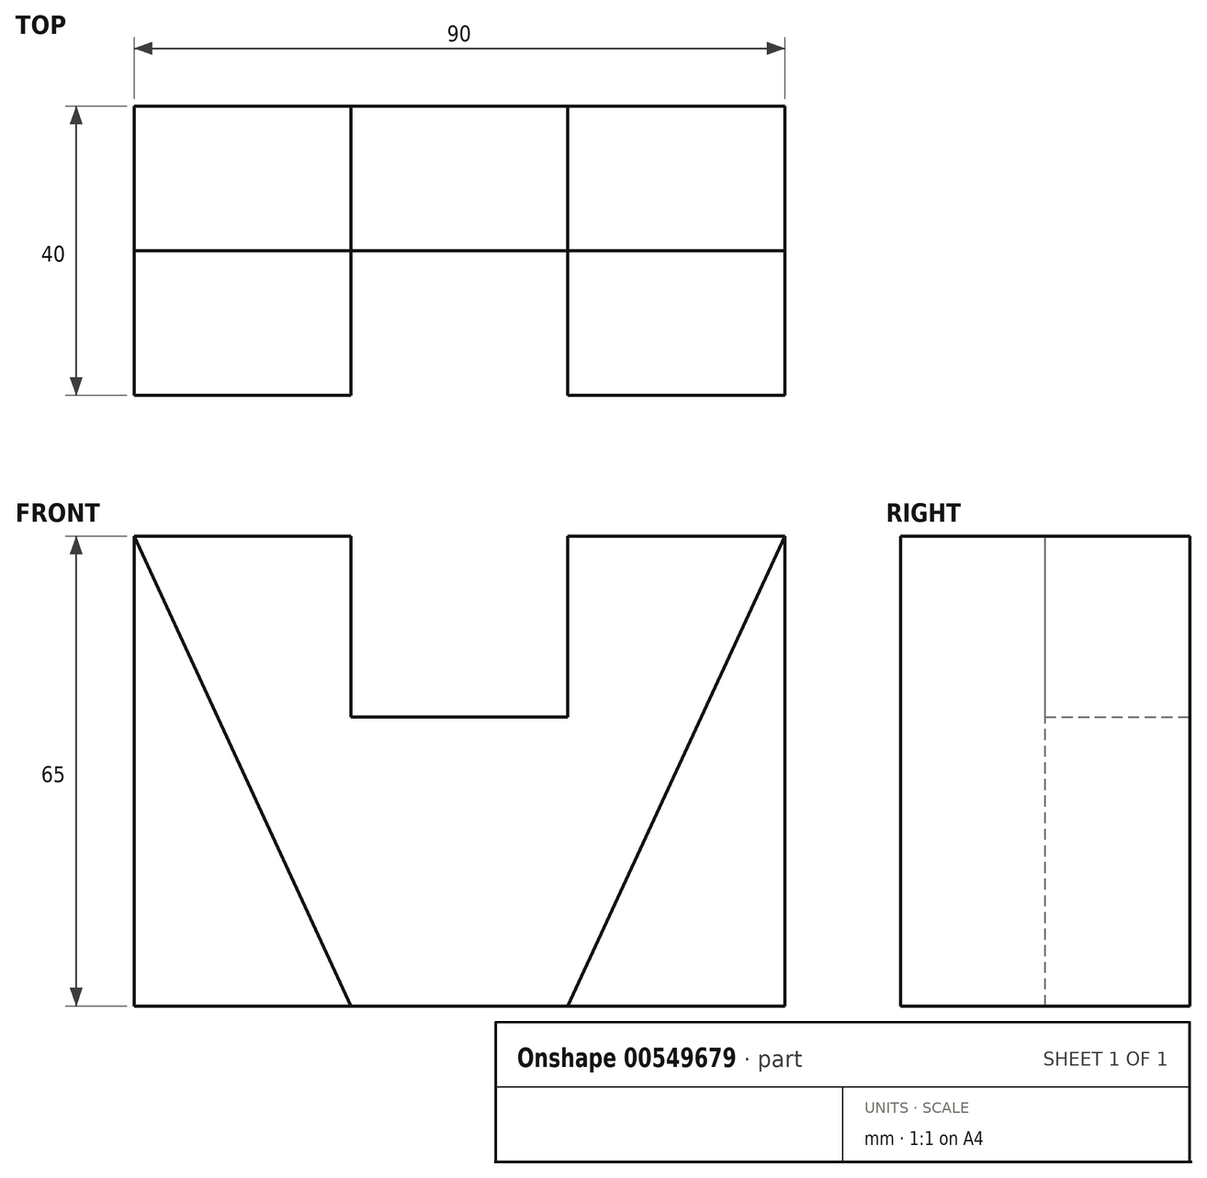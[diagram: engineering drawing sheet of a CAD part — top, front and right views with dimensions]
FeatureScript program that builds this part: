
annotation { "Feature Type Name" : "Feature", "Feature Type Description" : "" }
export const myFeature = defineFeature(function(context is Context, id is Id, definition is map)
    precondition{}
    {
        {
            var Q0;
            Q0=qCreatedBy(makeId("Front.planeOp"),FACE);
            var sketch = newSketch(context, id + "F0", { "sketchPlane" : qUnion([Q0])});
            skLineSegment(sketch, "E0.bottom", {"start": v(45, 32.5) * mm, "end": v(15, 32.5) * mm});
            skLineSegment(sketch, "E0.top", {"start": v(45, -32.5) * mm, "end": v(-45, -32.5) * mm});
            skLineSegment(sketch, "E0.left", {"start": v(45, 32.5) * mm, "end": v(45, -32.5) * mm});
            skLineSegment(sketch, "E0.right", {"start": v(-45, 32.5) * mm, "end": v(-45, -32.5) * mm});
            skPoint(sketch, "E0.middle", {"position": v(0, 0) * mm});
            skLineSegment(sketch, "E1.bottom", {"start": v(15, 7.5) * mm, "end": v(-15, 7.5) * mm});
            skLineSegment(sketch, "E1.left", {"start": v(15, 7.5) * mm, "end": v(15, 32.5) * mm});
            skLineSegment(sketch, "E1.right", {"start": v(-15, 7.5) * mm, "end": v(-15, 32.5) * mm});
            skPoint(sketch, "E1.middle", {"position": v(0, 32.5) * mm});
            skPoint(sketch, "E1.top.end.orphan", {"position": v(-15, 57.5) * mm});
            skPoint(sketch, "E2.orphan", {"position": v(15, 57.5) * mm});
            skLineSegment(sketch, "E3.trimOffspring", {"start": v(-15, 32.5) * mm, "end": v(-45, 32.5) * mm});
            skSolve(sketch);
        }
        {
            var Q0;
            Q0 = qSketchRegion(id + "F0", true);
            extrude(context, id + "F1", {"entities" : qUnion([Q0]), "depth" : (40 - 20) * mm, "offsetDistance" : 25 * mm});
        }
        {
            var Q0;
            Q0=makeQuery(id+"F1.opExtrude","CAP_FACE",FACE,{"disambiguationData":[OSD([sQuery(id+"F0.wireOp",EDGE,"E0.bottom"),sQuery(id+"F0.wireOp",EDGE,"E0.top"),sQuery(id+"F0.wireOp",EDGE,"E0.left"),sQuery(id+"F0.wireOp",EDGE,"E0.right"),sQuery(id+"F0.wireOp",EDGE,"E1.bottom"),sQuery(id+"F0.wireOp",EDGE,"E1.left"),sQuery(id+"F0.wireOp",EDGE,"E1.right"),sQuery(id+"F0.wireOp",EDGE,"E3.trimOffspring")])],"isStart":false});
            var sketch = newSketch(context, id + "F2", { "sketchPlane" : qUnion([Q0])});
            skLineSegment(sketch, "E4", {"start": v(-15, -32.5) * mm, "end": v(-45, 32.5) * mm});
            skLineSegment(sketch, "E5", {"start": v(15, -32.5) * mm, "end": v(45, 32.5) * mm});
            skSolve(sketch);
        }
        {
            var Q0;
            Q0 = qSketchRegion(id + "F2", true);
            var Q1;
            {var subQ0=sQuery(id+"F2.wireOp",EDGE,"E5");Q1=makeQuery(id+"F2.imprint","IMPRINT",FACE,{"disambiguationData":[TD([[makeQuery(id+"F2.imprint","IMPRINT",EDGE,{"derivedFrom":subQ0}),-1.0]])]});}
            var Q2;
            {var subQ0=sQuery(id+"F2.wireOp",EDGE,"E4");Q2=makeQuery(id+"F2.imprint","IMPRINT",FACE,{"disambiguationData":[TD([[makeQuery(id+"F2.imprint","IMPRINT",EDGE,{"derivedFrom":subQ0}),1.0]])]});}
            extrude(context, id + "F3", {"entities" : qUnion([Q0, Q1, Q2]), "operationType" : NewBodyOperationType.ADD, "depth" : (40 - 20) * mm, "offsetDistance" : 25 * mm});
        }
    });
